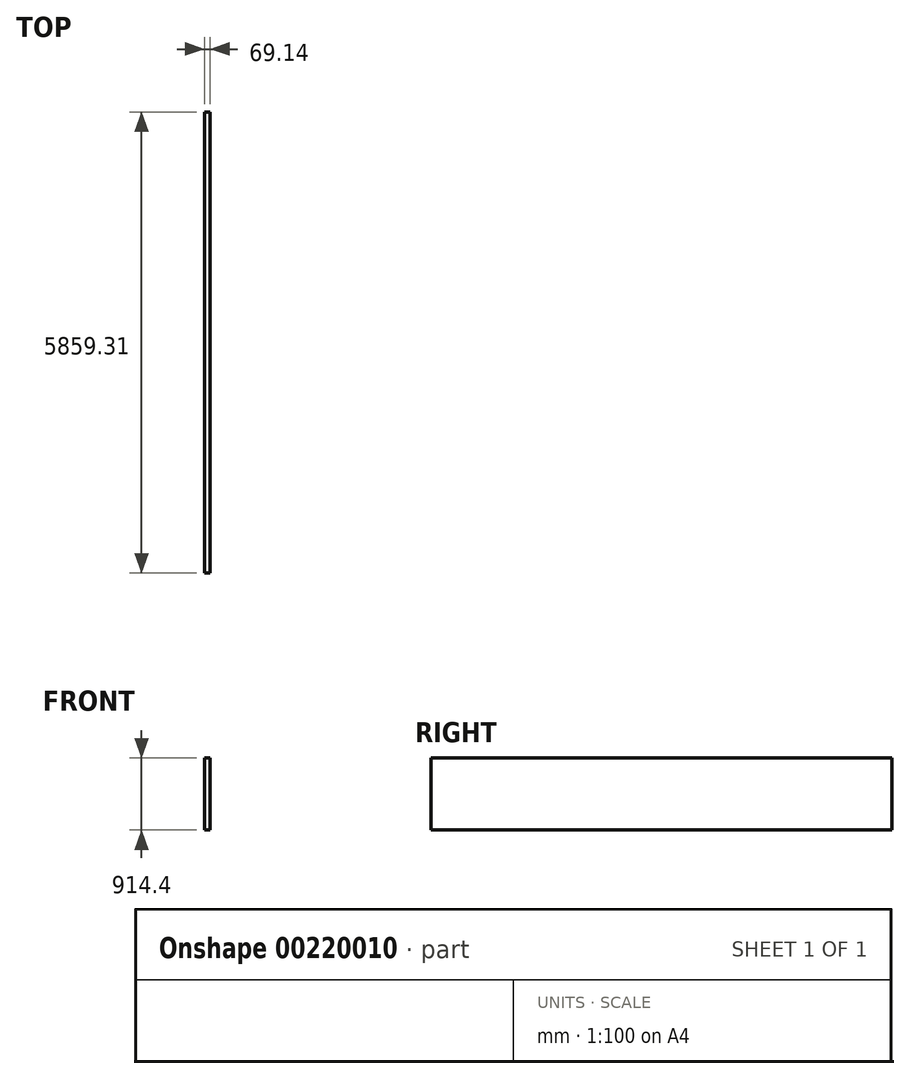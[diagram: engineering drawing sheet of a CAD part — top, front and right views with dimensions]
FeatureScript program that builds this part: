
annotation { "Feature Type Name" : "Feature", "Feature Type Description" : "" }
export const myFeature = defineFeature(function(context is Context, id is Id, definition is map)
    precondition{}
    {
        {
            var Q0;
            Q0=qCreatedBy(makeId("Right.planeOp"),FACE);
            var sketch = newSketch(context, id + "F0", { "sketchPlane" : qUnion([Q0])});
            skLineSegment(sketch, "E0.bottom", {"start": v(0, 0) * mm, "end": v(5859.3, 0) * mm});
            skLineSegment(sketch, "E0.top", {"start": v(0, 914.4) * mm, "end": v(5859.3, 914.4) * mm});
            skLineSegment(sketch, "E0.left", {"start": v(0, 0) * mm, "end": v(0, 914.4) * mm});
            skLineSegment(sketch, "E0.right", {"start": v(5859.3, 0) * mm, "end": v(5859.3, 914.4) * mm});
            skSolve(sketch);
        }
        {
            var Q0;
            Q0=makeQuery(id+"F0.imprint","IMPRINT",FACE,{"disambiguationData":[TD([[makeQuery(id+"F0.imprint","IMPRINT",EDGE,{"derivedFrom":sQuery(id+"F0.wireOp",EDGE,"E0.bottom")}),1.0]])]});
            extrude(context, id + "F1", {"entities" : qUnion([Q0]), "depth" : 69.14 * mm});
        }
    });
